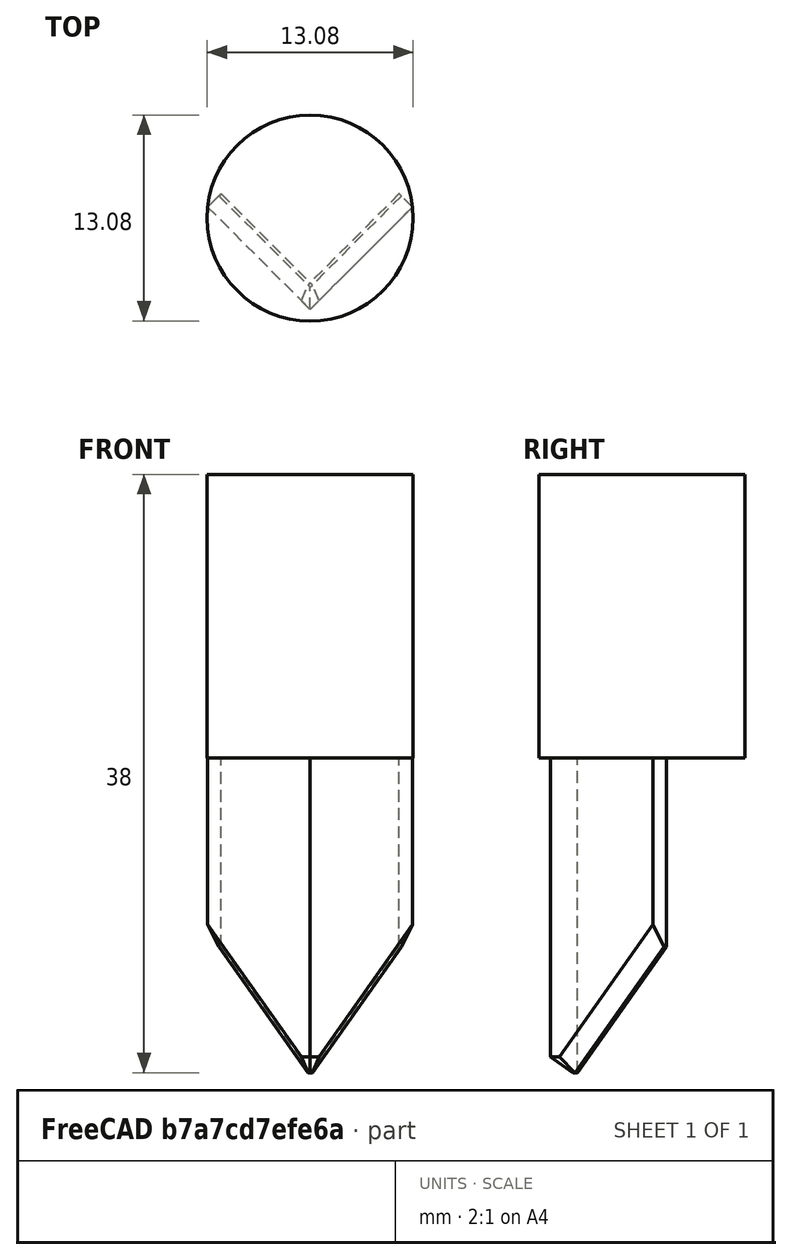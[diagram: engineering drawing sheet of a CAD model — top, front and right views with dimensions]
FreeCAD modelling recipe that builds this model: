
FCSTD DOCUMENT  (FreeCAD 0.19R)
Label: SaltScoop
License: All rights reserved
LicenseURL: http://en.wikipedia.org/wiki/All_rights_reserved
objects: Sketcher::SketchObject×3, PartDesign::Pad×2, PartDesign::Chamfer×2, PartDesign::Body×1, Mesh::Feature×1
note: 12 computed .brp shape members not serialized (recipe doc carries the construction recipe); baked Part::Feature solids carry a one-line shape summary decoded from their .brp

FEATURE [Sketcher::SketchObject] Sketch
  FullyConstrained = true
  MapMode = 5
  Support = -> [XY_Plane]
  sketch-geometry (6):
    g0: LineSegment StartX=-6.50538 StartY=6.50538 StartZ=0 EndX=0 EndY=0 EndZ=0
    g1: LineSegment StartX=0 StartY=0 StartZ=0 EndX=6.50538 EndY=6.50538 EndZ=0
    g2: LineSegment StartX=6.50538 StartY=6.50538 StartZ=0 EndX=5.65685 EndY=7.35391 EndZ=0
    g3: LineSegment StartX=5.65685 StartY=7.35391 StartZ=0 EndX=0 EndY=1.69706 EndZ=0
    g4: LineSegment StartX=0 StartY=1.69706 StartZ=0 EndX=-5.65685 EndY=7.35391 EndZ=0
    g5: LineSegment StartX=-5.65685 StartY=7.35391 StartZ=0 EndX=-6.50538 EndY=6.50538 EndZ=0
  constraints (15):
    c: Coincident(g0,g-1)
    c: Coincident(g0,g1)
    c: Coincident(g1,g2)
    c: Coincident(g2,g3)
    c: PointOnObject(g3,g-2)
    c: Coincident(g3,g4)
    c: Coincident(g4,g5)
    c: Coincident(g5,g0)
    c: Symmetric(g2,g4,g-2)
    c: Symmetric(g0,g1,g-2)
    c: Perpendicular(g3,g2)
    c: Perpendicular(g0,g5)
    c: Distance(g2) = 1.2
    c: Distance(g3) = 8
    c: Perpendicular(g4,g3)
FEATURE [PartDesign::Pad] Pad
  Direction = (1,1,1)
  Length = 20
  Length2 = 100
  Profile = -> Sketch
  Type = 0
FEATURE [Sketcher::SketchObject] Sketch001
  ExternalGeometry = -> [Pad]
  FullyConstrained = false
  MapMode = 5
  Placement = pos=(0,0,20) rot=(0,0,1;0rad)
  Support = -> [Pad]
  sketch-geometry (1):
    g0: Circle CenterX=0 CenterY=5.80829 CenterZ=0 NormalX=0 NormalY=0 NormalZ=1 AngleXU=0 Radius=6.54262
  constraints (2):
    c: PointOnObject(g0,g-2)
    c: PointOnObject(g-3,g0)
FEATURE [PartDesign::Pad] Pad001
  BaseFeature = -> Pad
  Direction = (1,1,1)
  Length = 18
  Length2 = 100
  Profile = -> Sketch001
  Type = 0
FEATURE [Sketcher::SketchObject] Sketch002
  FullyConstrained = false
  MapMode = 5
  Placement = pos=(0,0,0) rot=(0.862856,0.357407,0.357407;1.71777rad)
  Support = -> [Pad001]
  sketch-geometry (3):
    g0: LineSegment StartX=3.6e-15 StartY=0 StartZ=0 EndX=13.9629 EndY=7.20347 EndZ=0
    g1: LineSegment StartX=13.9629 StartY=7.20347 StartZ=0 EndX=13.9629 EndY=-18.8918 EndZ=0
    g2: LineSegment StartX=13.9629 StartY=-18.8918 StartZ=0 EndX=3.6e-15 EndY=0 EndZ=0
  constraints (5):
    c: Coincident(g-1,g0)
    c: Coincident(g0,g1)
    c: Vertical(g1)
    c: Coincident(g1,g2)
    c: Coincident(g2,g0)
FEATURE [PartDesign::Chamfer] Chamfer
  Angle = 45
  Base = -> Pad001 [Edge18,Edge23]
  BaseFeature = -> Pad001
  ChamferType = 0
  FlipDirection = false
  Size = 8
  Size2 = 1
  SupportTransform = false
FEATURE [PartDesign::Chamfer] Chamfer001
  Angle = 45
  Base = -> Chamfer [Edge17,Edge2,Edge4,Edge14]
  BaseFeature = -> Chamfer
  ChamferType = 0
  FlipDirection = false
  Size = 1
  Size2 = 1
  SupportTransform = false
FEATURE [PartDesign::Body] Body
  Group = -> [Sketch,Pad,Sketch001,Pad001,Sketch002,Chamfer,Chamfer001]
  Origin = -> Origin
  Tip = -> Chamfer001
FEATURE [Mesh::Feature] Mesh  label="Chamfer001 (Meshed)"
